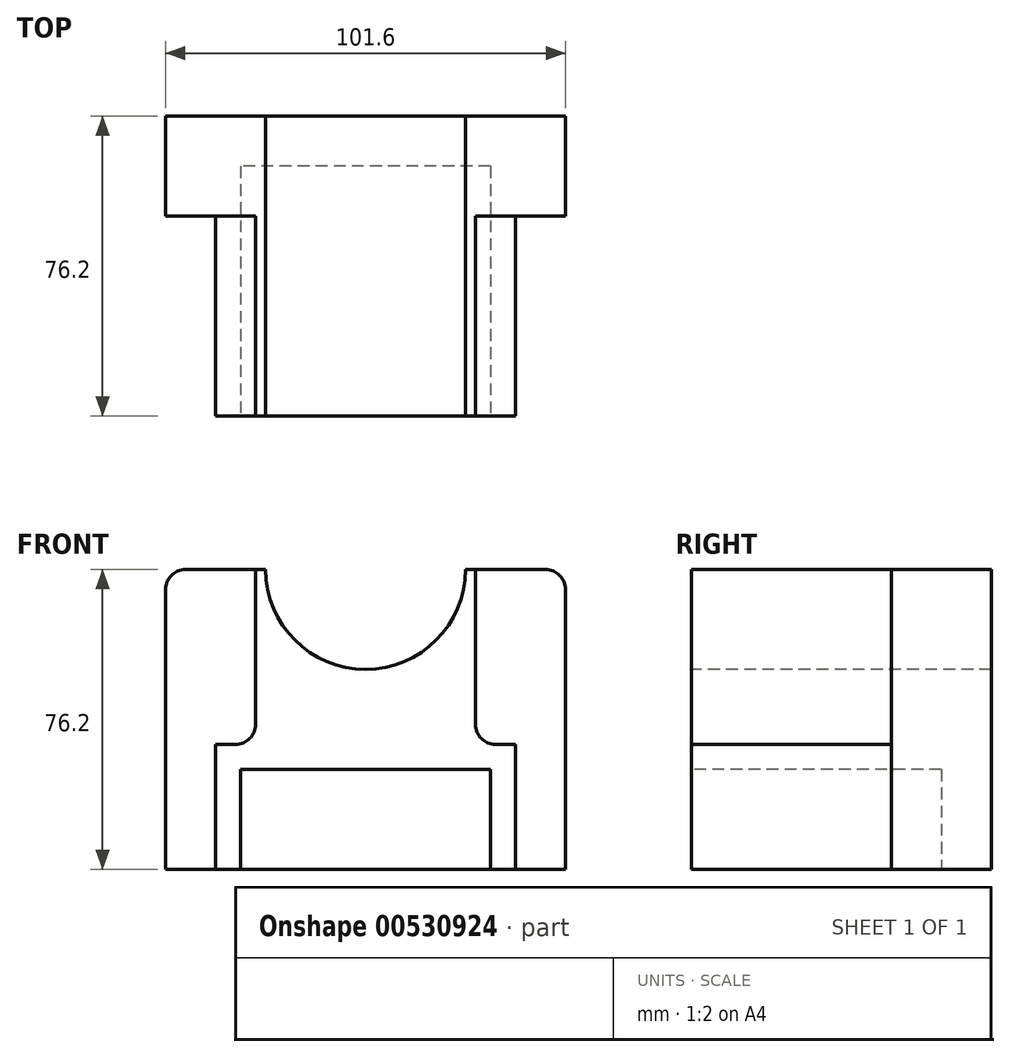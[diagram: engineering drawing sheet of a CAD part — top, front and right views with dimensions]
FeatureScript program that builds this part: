
annotation { "Feature Type Name" : "Feature", "Feature Type Description" : "" }
export const myFeature = defineFeature(function(context is Context, id is Id, definition is map)
    precondition{}
    {
        {
            var Q0;
            Q0=qCreatedBy(makeId("Front.planeOp"),FACE);
            var sketch = newSketch(context, id + "F0", { "sketchPlane" : qUnion([Q0])});
            skLineSegment(sketch, "E0.bottom", {"start": v(50.8, 38.1) * mm, "end": v(-50.8, 38.1) * mm});
            skLineSegment(sketch, "E0.top", {"start": v(50.8, -38.1) * mm, "end": v(-50.8, -38.1) * mm});
            skLineSegment(sketch, "E0.left", {"start": v(50.8, 38.1) * mm, "end": v(50.8, -38.1) * mm});
            skLineSegment(sketch, "E0.right", {"start": v(-50.8, 38.1) * mm, "end": v(-50.8, -38.1) * mm});
            skPoint(sketch, "E0.middle", {"position": v(0, 0) * mm});
            skSolve(sketch);
        }
        {
            var Q0;
            Q0=makeQuery(id+"F0.imprint","IMPRINT",FACE,{"disambiguationData":[TD([[makeQuery(id+"F0.imprint","IMPRINT",EDGE,{"derivedFrom":sQuery(id+"F0.wireOp",EDGE,"E0.bottom")}),1.0]])]});
            extrude(context, id + "F1", {"entities" : qUnion([Q0]), "depth" : 76.2 * mm, "offsetDistance" : 25.4 * mm});
        }
        {
            var Q0;
            Q0=makeQuery(id+"F1.opExtrude","CAP_FACE",FACE,{"disambiguationData":[OSD([sQuery(id+"F0.wireOp",EDGE,"E0.bottom"),sQuery(id+"F0.wireOp",EDGE,"E0.top"),sQuery(id+"F0.wireOp",EDGE,"E0.left"),sQuery(id+"F0.wireOp",EDGE,"E0.right")])],"isStart":false});
            var sketch = newSketch(context, id + "F2", { "sketchPlane" : qUnion([Q0])});
            skCircle(sketch, "E1", {"center": v(0, 38.1) * mm, "radius": 25.4 * mm});
            skLineSegment(sketch, "E2.bottom", {"start": v(31.75, -12.7) * mm, "end": v(-31.75, -12.7) * mm});
            skLineSegment(sketch, "E2.top", {"start": v(31.75, -63.5) * mm, "end": v(-31.75, -63.5) * mm});
            skLineSegment(sketch, "E2.left", {"start": v(31.75, -12.7) * mm, "end": v(31.75, -63.5) * mm});
            skLineSegment(sketch, "E2.right", {"start": v(-31.75, -12.7) * mm, "end": v(-31.75, -63.5) * mm});
            skPoint(sketch, "E2.middle", {"position": v(0, -38.1) * mm});
            skLineSegment(sketch, "E3.bottom", {"start": v(27.94, 38.1) * mm, "end": v(50.8, 38.1) * mm});
            skLineSegment(sketch, "E3.top", {"start": v(27.94, -6.35) * mm, "end": v(50.8, -6.35) * mm});
            skLineSegment(sketch, "E3.left", {"start": v(27.94, 38.1) * mm, "end": v(27.94, -6.35) * mm});
            skLineSegment(sketch, "E3.right", {"start": v(50.8, 38.1) * mm, "end": v(50.8, -6.35) * mm});
            skLineSegment(sketch, "E4.bottom", {"start": v(50.8, -38.1) * mm, "end": v(38.1, -38.1) * mm});
            skLineSegment(sketch, "E4.top", {"start": v(50.8, -6.35) * mm, "end": v(38.1, -6.35) * mm});
            skLineSegment(sketch, "E4.left", {"start": v(50.8, -38.1) * mm, "end": v(50.8, -6.35) * mm});
            skLineSegment(sketch, "E4.right", {"start": v(38.1, -38.1) * mm, "end": v(38.1, -6.35) * mm});
            skLineSegment(sketch, "E5.bottom", {"start": v(-50.8, 38.1) * mm, "end": v(-27.94, 38.1) * mm});
            skLineSegment(sketch, "E5.top", {"start": v(-50.8, -6.35) * mm, "end": v(-27.94, -6.35) * mm});
            skLineSegment(sketch, "E5.left", {"start": v(-50.8, 38.1) * mm, "end": v(-50.8, -6.35) * mm});
            skLineSegment(sketch, "E5.right", {"start": v(-27.94, 38.1) * mm, "end": v(-27.94, -6.35) * mm});
            skLineSegment(sketch, "E6.bottom", {"start": v(-50.8, -38.1) * mm, "end": v(-38.1, -38.1) * mm});
            skLineSegment(sketch, "E6.top", {"start": v(-50.8, -6.35) * mm, "end": v(-38.1, -6.35) * mm});
            skLineSegment(sketch, "E6.left", {"start": v(-50.8, -38.1) * mm, "end": v(-50.8, -6.35) * mm});
            skLineSegment(sketch, "E6.right", {"start": v(-38.1, -38.1) * mm, "end": v(-38.1, -6.35) * mm});
            skSolve(sketch);
        }
        {
            var Q0;
            {var subQ0=sQuery(id+"F2.wireOp",EDGE,"E1");var subQ1=makeQuery(id+"F1.opExtrude","CAP_EDGE",EDGE,{"disambiguationData":[OSD([sQuery(id+"F0.wireOp",EDGE,"E0.bottom")])],"isStart":false});var subQ2=makeQuery(id+"F2.imprint","INTERSECT",VERTEX,{"disambiguationData":[OD(0.0)],"derivedFrom":[subQ1,subQ0]});Q0=makeQuery(id+"F2.imprint","IMPRINT",FACE,{"disambiguationData":[TD([[makeQuery(id+"F2.imprint","IMPRINT",EDGE,{"disambiguationData":[TD([[subQ2,1.0]])],"derivedFrom":subQ0}),1.0]])]});}
            extrude(context, id + "F3", {"entities" : qUnion([Q0]), "operationType" : NewBodyOperationType.REMOVE, "endBound" : BoundingType.THROUGH_ALL, "oppositeDirection" : true, "depth" : 25.4 * mm, "offsetDistance" : 25.4 * mm});
        }
        {
            var Q0;
            {var subQ0=sQuery(id+"F2.wireOp",EDGE,"E2.bottom");Q0=makeQuery(id+"F2.imprint","IMPRINT",FACE,{"disambiguationData":[TD([[makeQuery(id+"F2.imprint","IMPRINT",EDGE,{"derivedFrom":subQ0}),1.0]])]});}
            extrude(context, id + "F4", {"entities" : qUnion([Q0]), "operationType" : NewBodyOperationType.REMOVE, "oppositeDirection" : true, "depth" : 63.5 * mm, "offsetDistance" : 25.4 * mm});
        }
        {
            var Q0;
            Q0=makeQuery(id+"F2.imprint","IMPRINT",FACE,{"disambiguationData":[TD([[makeQuery(id+"F2.imprint","IMPRINT",EDGE,{"derivedFrom":sQuery(id+"F2.wireOp",EDGE,"E3.bottom")}),1.0]])]});
            var Q1;
            Q1=makeQuery(id+"F2.imprint","IMPRINT",FACE,{"disambiguationData":[TD([[makeQuery(id+"F2.imprint","IMPRINT",EDGE,{"derivedFrom":sQuery(id+"F2.wireOp",EDGE,"E4.bottom")}),-1.0]])]});
            var Q2;
            Q2=makeQuery(id+"F2.imprint","IMPRINT",FACE,{"disambiguationData":[TD([[makeQuery(id+"F2.imprint","IMPRINT",EDGE,{"derivedFrom":sQuery(id+"F2.wireOp",EDGE,"E5.bottom")}),1.0]])]});
            var Q3;
            Q3=makeQuery(id+"F2.imprint","IMPRINT",FACE,{"disambiguationData":[TD([[makeQuery(id+"F2.imprint","IMPRINT",EDGE,{"derivedFrom":sQuery(id+"F2.wireOp",EDGE,"E6.bottom")}),-1.0]])]});
            extrude(context, id + "F5", {"entities" : qUnion([Q0, Q1, Q2, Q3]), "operationType" : NewBodyOperationType.REMOVE, "oppositeDirection" : true, "depth" : 50.8 * mm, "offsetDistance" : 25.4 * mm});
        }
        {
            var Q0;
            Q0=makeQuery(id+"F5.boolean.opBoolean","COPY",EDGE,{"derivedFrom":makeQuery(id+"F5.opExtrude","SWEPT_EDGE",EDGE,{"disambiguationData":[OSD([sQuery(id+"F2.wireOp",EDGE,"E3.top"),sQuery(id+"F2.wireOp",EDGE,"E3.left")])]})});
            var Q1;
            Q1=makeQuery(id+"F5.boolean.opBoolean","COPY",EDGE,{"derivedFrom":makeQuery(id+"F5.opExtrude","SWEPT_EDGE",EDGE,{"disambiguationData":[OSD([sQuery(id+"F2.wireOp",EDGE,"E5.top"),sQuery(id+"F2.wireOp",EDGE,"E5.right")])]})});
            fillet(context, id + "F6", {"entities" : qUnion([Q0, Q1]), "radius" : 5.08 * mm, "tangentPropagation" : true, "allowEdgeOverflow" : false});
        }
        {
            var Q0;
            Q0=makeQuery(id+"F1.opExtrude","SWEPT_EDGE",EDGE,{"disambiguationData":[OSD([sQuery(id+"F0.wireOp",EDGE,"E0.bottom"),sQuery(id+"F0.wireOp",EDGE,"E0.left")])]});
            var Q1;
            Q1=makeQuery(id+"F1.opExtrude","SWEPT_EDGE",EDGE,{"disambiguationData":[OSD([sQuery(id+"F0.wireOp",EDGE,"E0.bottom"),sQuery(id+"F0.wireOp",EDGE,"E0.right")])]});
            fillet(context, id + "F7", {"entities" : qUnion([Q0, Q1]), "radius" : 5.08 * mm, "tangentPropagation" : true, "allowEdgeOverflow" : false});
        }
    });
